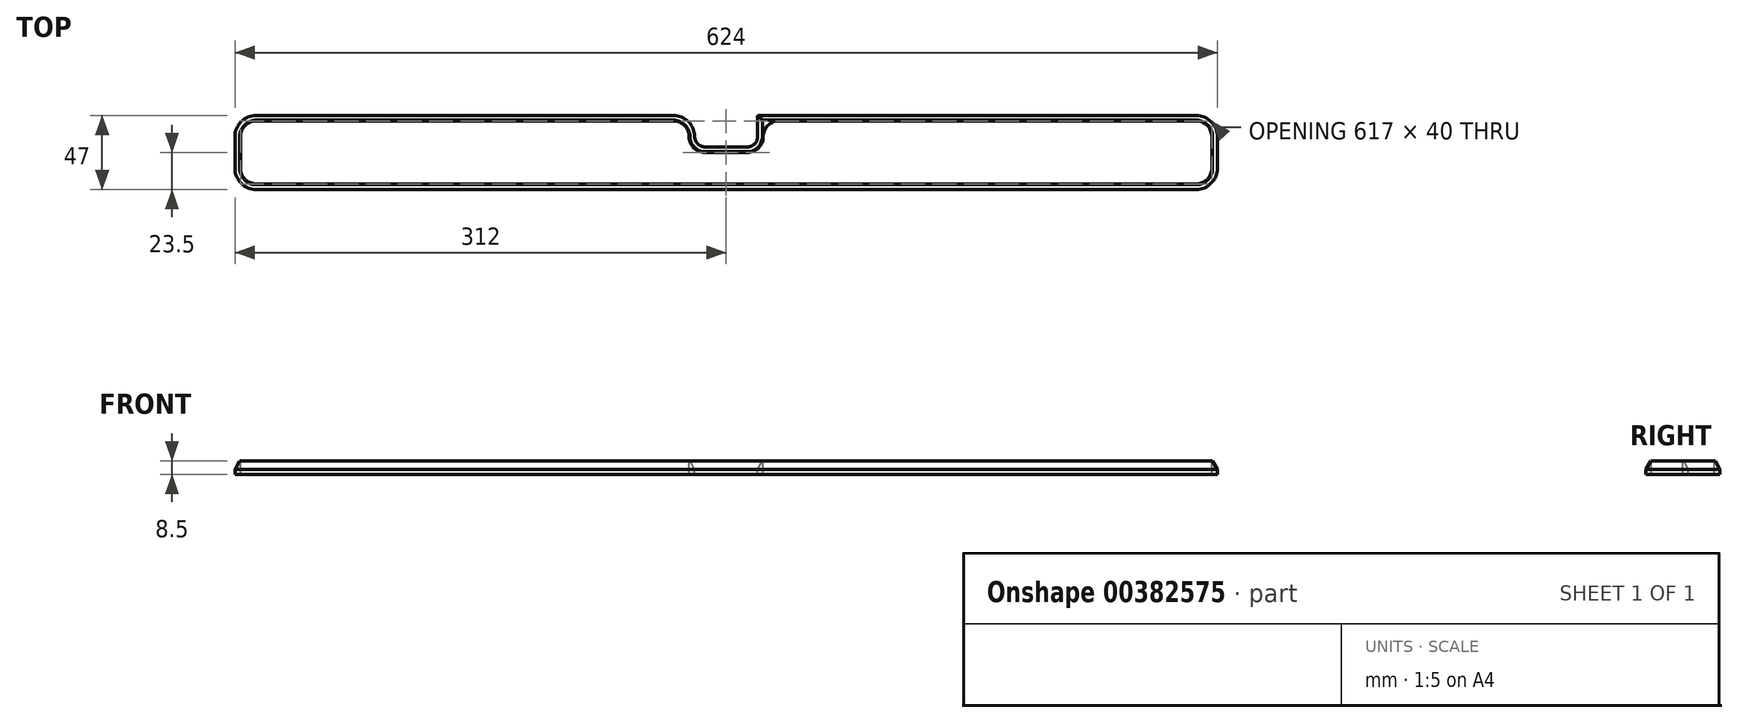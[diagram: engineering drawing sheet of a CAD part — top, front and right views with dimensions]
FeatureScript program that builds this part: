
annotation { "Feature Type Name" : "Feature", "Feature Type Description" : "" }
export const myFeature = defineFeature(function(context is Context, id is Id, definition is map)
    precondition{}
    {
        {
            var Q0;
            Q0=qCreatedBy(makeId("Top.planeOp"),FACE);
            var sketch = newSketch(context, id + "F0", { "sketchPlane" : qUnion([Q0])});
            skLineSegment(sketch, "E0.bottom", {"start": v(298.5, -23.5) * mm, "end": v(-298.5, -23.5) * mm});
            skLineSegment(sketch, "E0.top", {"start": v(298.5, 23.5) * mm, "end": v(-298.5, 23.5) * mm});
            skLineSegment(sketch, "E0.left", {"start": v(312, -10) * mm, "end": v(312, 10) * mm});
            skLineSegment(sketch, "E0.right", {"start": v(-312, -10) * mm, "end": v(-312, 10) * mm});
            skPoint(sketch, "E0.middle", {"position": v(0, 0) * mm});
            skPoint(sketch, "E1.visualSharp", {"position": v(-312, 23.5) * mm});
            skArc(sketch, "E1.filletArc", {"start": v(-298.5, 23.5) * mm, "mid": v(-308.05, 19.55) * mm, "end": v(-312, 10) * mm});
            skPoint(sketch, "E2.visualSharp", {"position": v(-312, -23.5) * mm});
            skArc(sketch, "E2.filletArc", {"start": v(-312, -10) * mm, "mid": v(-308.05, -19.55) * mm, "end": v(-298.5, -23.5) * mm});
            skPoint(sketch, "E3.visualSharp", {"position": v(312, -23.5) * mm});
            skArc(sketch, "E3.filletArc", {"start": v(298.5, -23.5) * mm, "mid": v(308.05, -19.55) * mm, "end": v(312, -10) * mm});
            skPoint(sketch, "E4.visualSharp", {"position": v(312, 23.5) * mm});
            skArc(sketch, "E4.filletArc", {"start": v(312, 10) * mm, "mid": v(308.05, 19.55) * mm, "end": v(298.5, 23.5) * mm});
            skSolve(sketch);
        }
        {
            var Q0;
            Q0=makeQuery(id+"F0.imprint","IMPRINT",FACE,{"disambiguationData":[TD([[makeQuery(id+"F0.imprint","IMPRINT",EDGE,{"derivedFrom":sQuery(id+"F0.wireOp",EDGE,"E0.bottom")}),-1.0]])]});
            extrude(context, id + "F1", {"entities" : qUnion([Q0]), "depth" : 8.5 * mm});
        }
        {
            var Q0;
            Q0=makeQuery(id+"F1.opExtrude","CAP_FACE",FACE,{"disambiguationData":[OSD([sQuery(id+"F0.wireOp",EDGE,"E0.bottom"),sQuery(id+"F0.wireOp",EDGE,"E0.top"),sQuery(id+"F0.wireOp",EDGE,"E0.left"),sQuery(id+"F0.wireOp",EDGE,"E0.right")])],"isStart":false});
            var sketch = newSketch(context, id + "F2", { "sketchPlane" : qUnion([Q0])});
            skLineSegment(sketch, "E5", {"start": v(0, 23.5) * mm, "end": v(0, -23.5) * mm, "construction": true});
            skLineSegment(sketch, "E6.bottom", {"start": v(13.5, 3.5) * mm, "end": v(-13.5, 3.5) * mm});
            skLineSegment(sketch, "E6.top", {"start": v(20, 23.5) * mm, "end": v(-20, 23.5) * mm});
            skLineSegment(sketch, "E6.left", {"start": v(20, 10) * mm, "end": v(20, 23.5) * mm});
            skLineSegment(sketch, "E6.right", {"start": v(-20, 10) * mm, "end": v(-20, 23.5) * mm});
            skPoint(sketch, "E6.middle", {"position": v(0, 13.5) * mm});
            skPoint(sketch, "E7.visualSharp", {"position": v(20, 3.5) * mm});
            skArc(sketch, "E7.filletArc", {"start": v(13.5, 3.5) * mm, "mid": v(18.1, 5.4) * mm, "end": v(20, 10) * mm});
            skPoint(sketch, "E8.visualSharp", {"position": v(-20, 3.5) * mm});
            skArc(sketch, "E8.filletArc", {"start": v(-20, 10) * mm, "mid": v(-18.1, 5.4) * mm, "end": v(-13.5, 3.5) * mm});
            skSolve(sketch);
        }
        {
            var Q0;
            Q0=makeQuery(id+"F2.imprint","IMPRINT",FACE,{"disambiguationData":[TD([[makeQuery(id+"F2.imprint","IMPRINT",EDGE,{"derivedFrom":sQuery(id+"F2.wireOp",EDGE,"E6.bottom")}),-1.0]])]});
            extrude(context, id + "F3", {"entities" : qUnion([Q0]), "operationType" : NewBodyOperationType.REMOVE, "endBound" : BoundingType.THROUGH_ALL, "oppositeDirection" : true, "depth" : 25.4 * mm});
        }
        {
            var Q0;
            Q0=makeQuery(id+"F1.opExtrude","CAP_FACE",FACE,{"disambiguationData":[OSD([sQuery(id+"F0.wireOp",EDGE,"E0.bottom"),sQuery(id+"F0.wireOp",EDGE,"E0.top"),sQuery(id+"F0.wireOp",EDGE,"E0.left"),sQuery(id+"F0.wireOp",EDGE,"E0.right")])],"isStart":false});
            var sketch = newSketch(context, id + "F4", { "sketchPlane" : qUnion([Q0])});
            skLineSegment(sketch, "E9", {"start": v(-308.5, -10) * mm, "end": v(-308.5, 10) * mm});
            skLineSegment(sketch, "E10", {"start": v(-298.5, 20) * mm, "end": v(-33.5, 20) * mm});
            skLineSegment(sketch, "E11", {"start": v(-23.5, 10) * mm, "end": v(-23.5, 10) * mm});
            skLineSegment(sketch, "E12", {"start": v(-13.5, 0) * mm, "end": v(13.5, 0) * mm});
            skLineSegment(sketch, "E13", {"start": v(23.5, 10) * mm, "end": v(23.5, 10) * mm});
            skLineSegment(sketch, "E14", {"start": v(33.5, 20) * mm, "end": v(298.5, 20) * mm});
            skLineSegment(sketch, "E15", {"start": v(-298.5, -20) * mm, "end": v(298.5, -20) * mm});
            skLineSegment(sketch, "E16", {"start": v(308.5, -10) * mm, "end": v(308.5, 10) * mm});
            skPoint(sketch, "E17.visualSharp", {"position": v(-23.5, 20) * mm});
            skArc(sketch, "E17.filletArc", {"start": v(-23.5, 10) * mm, "mid": v(-26.43, 17.07) * mm, "end": v(-33.5, 20) * mm});
            skPoint(sketch, "E18.visualSharp", {"position": v(-23.5, 0) * mm});
            skArc(sketch, "E18.filletArc", {"start": v(-23.5, 10) * mm, "mid": v(-20.57, 2.93) * mm, "end": v(-13.5, 0) * mm});
            skPoint(sketch, "E19.visualSharp", {"position": v(23.5, 0) * mm});
            skArc(sketch, "E19.filletArc", {"start": v(13.5, 0) * mm, "mid": v(20.57, 2.93) * mm, "end": v(23.5, 10) * mm});
            skPoint(sketch, "E20.visualSharp", {"position": v(23.5, 20) * mm});
            skArc(sketch, "E20.filletArc", {"start": v(33.5, 20) * mm, "mid": v(26.43, 17.07) * mm, "end": v(23.5, 10) * mm});
            skPoint(sketch, "E21.visualSharp", {"position": v(308.5, 20) * mm});
            skArc(sketch, "E21.filletArc", {"start": v(308.5, 10) * mm, "mid": v(305.57, 17.07) * mm, "end": v(298.5, 20) * mm});
            skPoint(sketch, "E22.visualSharp", {"position": v(308.5, -20) * mm});
            skArc(sketch, "E22.filletArc", {"start": v(298.5, -20) * mm, "mid": v(305.57, -17.07) * mm, "end": v(308.5, -10) * mm});
            skPoint(sketch, "E23.visualSharp", {"position": v(-308.5, -20) * mm});
            skArc(sketch, "E23.filletArc", {"start": v(-308.5, -10) * mm, "mid": v(-305.57, -17.07) * mm, "end": v(-298.5, -20) * mm});
            skPoint(sketch, "E24.visualSharp", {"position": v(-308.5, 20) * mm});
            skArc(sketch, "E24.filletArc", {"start": v(-298.5, 20) * mm, "mid": v(-305.57, 17.07) * mm, "end": v(-308.5, 10) * mm});
            skSolve(sketch);
        }
        {
            var Q0;
            Q0 = qSketchRegion(id + "F4", true);
            extrude(context, id + "F5", {"entities" : qUnion([Q0]), "operationType" : NewBodyOperationType.REMOVE, "endBound" : BoundingType.THROUGH_ALL, "oppositeDirection" : true, "depth" : 25.4 * mm});
        }
        {
            var Q0;
            Q0=makeQuery(id+"F3.boolean.opBoolean","COPY",EDGE,{"derivedFrom":makeQuery(id+"F3.opExtrude","SWEPT_EDGE",EDGE,{"disambiguationData":[OSD([sQuery(id+"F0.wireOp",EDGE,"E0.top"),sQuery(id+"F2.wireOp",EDGE,"E6.top"),sQuery(id+"F2.wireOp",EDGE,"E6.right")])]})});
            var Q1;
            Q1=makeQuery(id+"F3.boolean.opBoolean","COPY",EDGE,{"derivedFrom":makeQuery(id+"F3.opExtrude","SWEPT_EDGE",EDGE,{"disambiguationData":[OSD([sQuery(id+"F0.wireOp",EDGE,"E0.top"),sQuery(id+"F2.wireOp",EDGE,"E6.top"),sQuery(id+"F2.wireOp",EDGE,"E6.left")])]})});
            fillet(context, id + "F6", {"entities" : qUnion([Q0, Q1]), "radius" : 13.5 * mm, "tangentPropagation" : true, "allowEdgeOverflow" : false});
        }
        {
            var Q0;
            {var subQ0=sQuery(id+"F0.wireOp",EDGE,"E4.filletArc");var subQ1=sQuery(id+"F0.wireOp",EDGE,"E0.top");Q0=makeQuery(id+"F3.boolean.opBoolean","SPLIT",EDGE,{"disambiguationData":[TD([makeQuery(id+"F1.opExtrude","SWEPT_FACE",FACE,{"disambiguationData":[OSD([subQ0])]})])],"derivedFrom":makeQuery(id+"F1.opExtrude","CAP_EDGE",EDGE,{"disambiguationData":[OSD([subQ1])],"isStart":false})});}
            chamfer(context, id + "F7", {"entities" : qUnion([Q0]), "chamferType" : ChamferType.OFFSET_ANGLE, "width" : 3 * mm, "oppositeDirection" : false, "angle" : 60 * degree, "tangentPropagation" : true});
        }
    });
